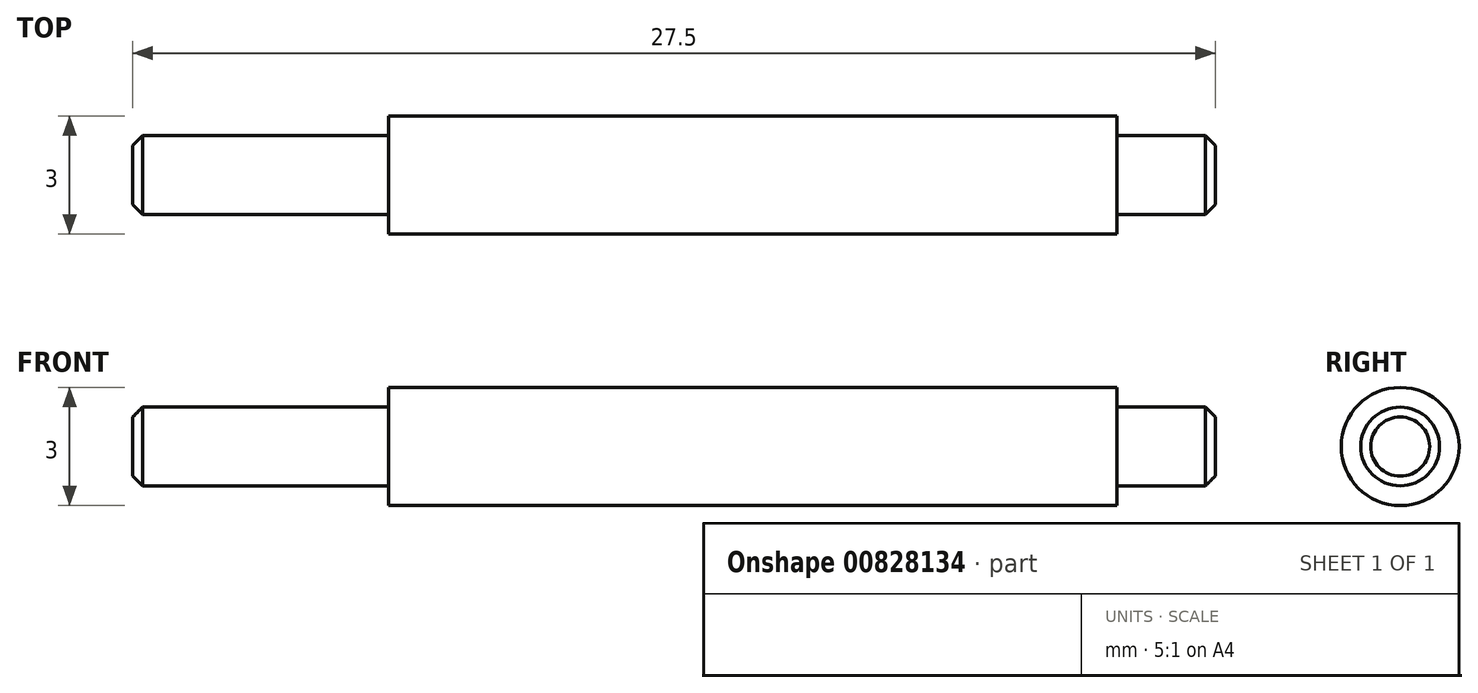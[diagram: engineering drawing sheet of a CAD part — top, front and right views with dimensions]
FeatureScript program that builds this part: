
annotation { "Feature Type Name" : "Feature", "Feature Type Description" : "" }
export const myFeature = defineFeature(function(context is Context, id is Id, definition is map)
    precondition{}
    {
        {
            var Q0;
            Q0=qCreatedBy(makeId("Front.planeOp"),FACE);
            var sketch = newSketch(context, id + "F0", { "sketchPlane" : qUnion([Q0])});
            skLineSegment(sketch, "E0", {"start": v(-14.55, 0) * mm, "end": v(31.09, 0) * mm, "construction": true});
            skLineSegment(sketch, "E1", {"start": v(0, 0) * mm, "end": v(0, 1) * mm});
            skLineSegment(sketch, "E2", {"start": v(0, 1) * mm, "end": v(6.5, 1) * mm});
            skLineSegment(sketch, "E3", {"start": v(6.5, 1) * mm, "end": v(6.5, 1.5) * mm});
            skLineSegment(sketch, "E4", {"start": v(6.5, 1.5) * mm, "end": v(25, 1.5) * mm});
            skLineSegment(sketch, "E5", {"start": v(25, 1.5) * mm, "end": v(25, 1) * mm});
            skLineSegment(sketch, "E6", {"start": v(25, 1) * mm, "end": v(27.5, 1) * mm});
            skLineSegment(sketch, "E7", {"start": v(27.5, 1) * mm, "end": v(27.5, 0) * mm});
            skLineSegment(sketch, "E8", {"start": v(27.5, 0) * mm, "end": v(0, 0) * mm});
            skSolve(sketch);
        }
        {
            var Q0;
            Q0 = qSketchRegion(id + "F0", true);
            var Q1;
            Q1=sQuery(id+"F0.wireOp",EDGE,"E0");
            revolve(context, id + "F1", {"surfaceOperationType" : NewSurfaceOperationType.NEW, "entities" : qUnion([Q0]), "axis" : qUnion([Q1]), "revolveType" : RevolveType.FULL});
        }
        {
            var Q0;
            Q0=makeQuery(id+"F1.opRevolve","SWEPT_EDGE",EDGE,{"disambiguationData":[OSD([sQuery(id+"F0.wireOp",EDGE,"E1"),sQuery(id+"F0.wireOp",EDGE,"E2")])]});
            var Q1;
            Q1=makeQuery(id+"F1.opRevolve","SWEPT_EDGE",EDGE,{"disambiguationData":[OSD([sQuery(id+"F0.wireOp",EDGE,"E6"),sQuery(id+"F0.wireOp",EDGE,"E7")])]});
            chamfer(context, id + "F2", {"entities" : qUnion([Q0, Q1]), "width" : 0.25 * mm, "tangentPropagation" : true});
        }
    });
